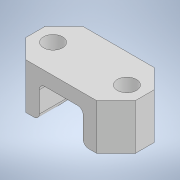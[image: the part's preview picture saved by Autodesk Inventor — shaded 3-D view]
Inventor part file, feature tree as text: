
AUTODESK INVENTOR PART (.ipt)
format: ipt  version: 2022 (Build 260153000, 153)  size: 201,728 bytes
history: native  units: mm
features: projected_geometry x6, sketch x5, extrude x4, thicken_offset x2, plane x1, hole x1, fillet x1, chamfer x1
ambient origin geometry x8: Origin, YZ Plane, XZ Plane, XY Plane, X Axis, Y Axis, Z Axis, Center Point
bodies: Solid1 (feature_tree)
feature tree (21):
  extrude  "Extrusion1"  Depth=16.0mm
  plane  "Work Plane1"
  extrude  "Extrusion3"  Depth=12.0mm
  hole  "Hole1"  [1 undecoded]
  fillet  "Fillet1"  [1 undecoded]
  extrude  "Extrusion4"  Depth=8.0mm
  chamfer  "Chamfer2"  Distance=3.0mm Angle=30.0deg
  extrude  "Extrusion5"  Depth=2.0mm
  thicken_offset  "Thicken1"
  thicken_offset  "Thicken2"
  sketch  "Sketch1"  dims[d0=11.7mm d1=16.0mm]
  sketch  "Sketch3"  dims[d2=12.0mm d3=12.0mm]
  projected_geometry  "Projected Loop3"
  projected_geometry  "Projected Loop4"
  sketch  "Sketch4"  dims[d4=5.0mm d5=21.0mm d6=0.0mm d12=-3.0mm]
  projected_geometry  "Projected Loop5"
  projected_geometry  "Projected Loop6"
  sketch  "Sketch5"  dims[d13=8.0mm d14=8.0mm]
  projected_geometry  "Projected Loop7"
  sketch  "Sketch6"  dims[d15=27.0mm d16=3.0mm d17=30.0deg d18=3.4mm d19=6.0mm d20=6.3mm d21=2.0mm d22=90.0deg d23=8.0mm d24=0.0mm d28=2.0mm d29=7.0mm d30=6.0mm d31=0.0mm d32=1.8mm d33=2.0mm d34=45.0deg d35=135.0deg d36=45.0deg d37=5.0mm d38=0.0mm d39=0.0mm d40=0.2mm d41=0.2mm d42=0.2mm d43=0.2mm]
  projected_geometry  "Projected Loop8"
note: 2 required parameter values undecoded (feature->parameter linkage not recoverable at this tier; creation-order binding heuristic only, values carry confidence <= 0.55)
